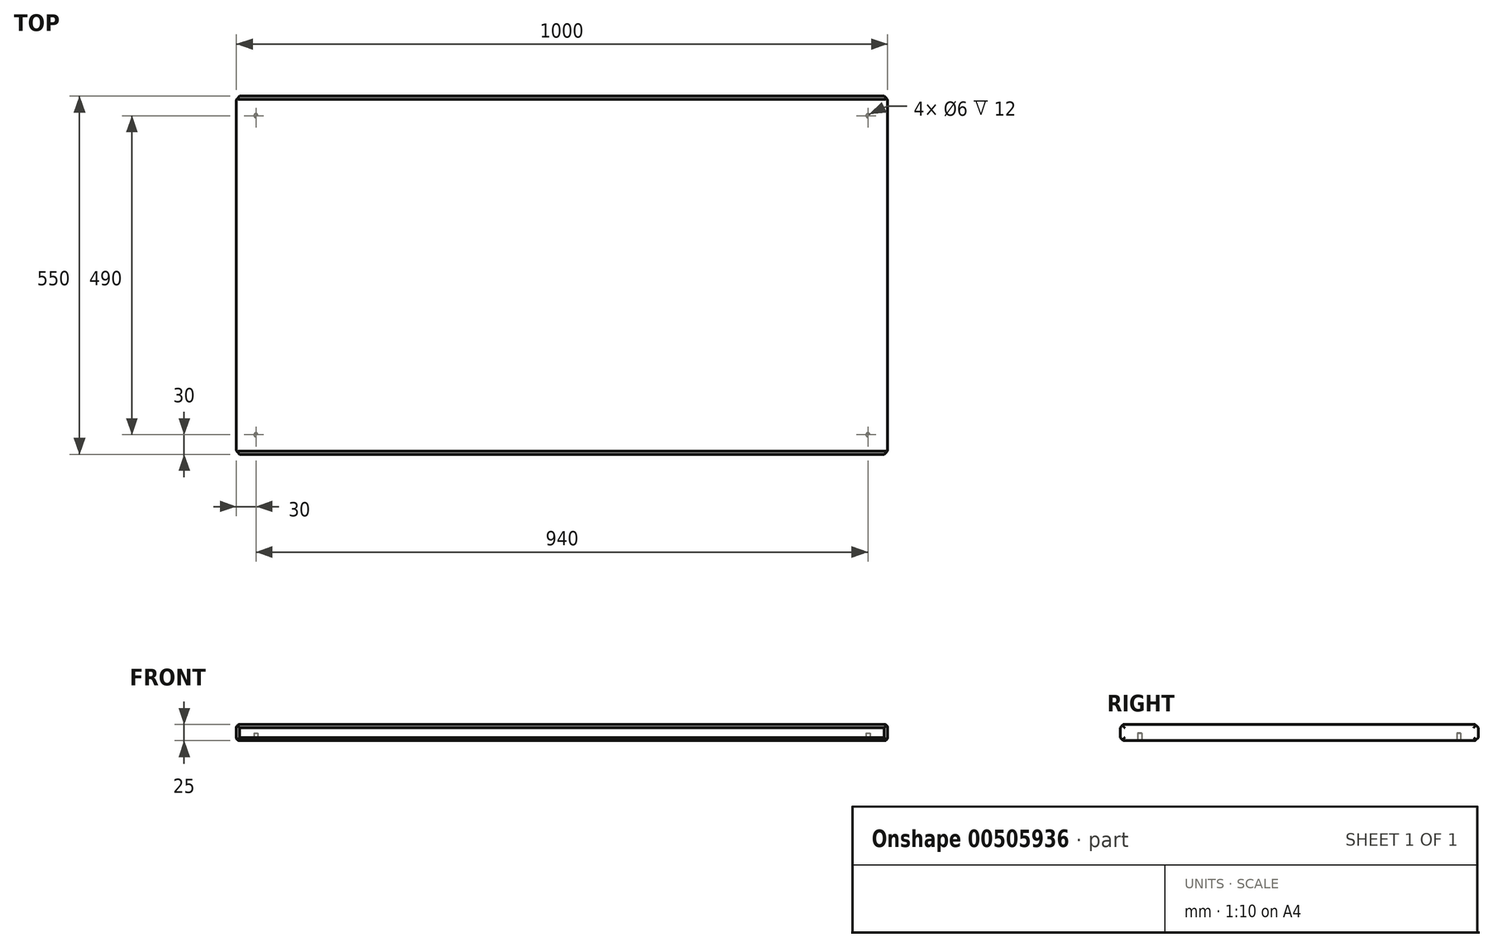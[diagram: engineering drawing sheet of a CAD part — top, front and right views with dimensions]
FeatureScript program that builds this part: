
annotation { "Feature Type Name" : "Feature", "Feature Type Description" : "" }
export const myFeature = defineFeature(function(context is Context, id is Id, definition is map)
    precondition{}
    {
        {
            var Q0;
            Q0=qCreatedBy(makeId("Top.planeOp"),FACE);
            var sketch = newSketch(context, id + "F0", { "sketchPlane" : qUnion([Q0])});
            skLineSegment(sketch, "E0.bottom", {"start": v(500, -275) * mm, "end": v(-500, -275) * mm});
            skLineSegment(sketch, "E0.top", {"start": v(500, 275) * mm, "end": v(-500, 275) * mm});
            skLineSegment(sketch, "E0.left", {"start": v(500, -275) * mm, "end": v(500, 275) * mm});
            skLineSegment(sketch, "E0.right", {"start": v(-500, -275) * mm, "end": v(-500, 275) * mm});
            skPoint(sketch, "E0.middle", {"position": v(0, 0) * mm});
            skSolve(sketch);
        }
        {
            var Q0;
            Q0=makeQuery(id+"F0.imprint","IMPRINT",FACE,{"disambiguationData":[TD([[makeQuery(id+"F0.imprint","IMPRINT",EDGE,{"derivedFrom":sQuery(id+"F0.wireOp",EDGE,"E0.bottom")}),-1.0]])]});
            extrude(context, id + "F1", {"entities" : qUnion([Q0]), "depth" : 25 * mm, "offsetDistance" : 25 * mm});
        }
        {
            var Q0;
            Q0=makeQuery(id+"F1.opExtrude","SWEPT_FACE",FACE,{"disambiguationData":[OSD([sQuery(id+"F0.wireOp",EDGE,"E0.bottom")])]});
            chamfer(context, id + "F2", {"entities" : qUnion([Q0]), "width" : 5 * mm, "tangentPropagation" : true});
        }
        {
            var Q0;
            Q0=makeQuery(id+"F1.opExtrude","SWEPT_FACE",FACE,{"disambiguationData":[OSD([sQuery(id+"F0.wireOp",EDGE,"E0.top")])]});
            chamfer(context, id + "F3", {"entities" : qUnion([Q0]), "width" : 5 * mm, "tangentPropagation" : true});
        }
        {
            var Q0;
            Q0=makeQuery(id+"F1.opExtrude","SWEPT_FACE",FACE,{"disambiguationData":[OSD([sQuery(id+"F0.wireOp",EDGE,"E0.right")])]});
            fillet(context, id + "F4", {"entities" : qUnion([Q0]), "radius" : 5 * mm, "tangentPropagation" : true, "allowEdgeOverflow" : false});
        }
        {
            var Q0;
            Q0=makeQuery(id+"F1.opExtrude","SWEPT_FACE",FACE,{"disambiguationData":[OSD([sQuery(id+"F0.wireOp",EDGE,"E0.left")])]});
            fillet(context, id + "F5", {"entities" : qUnion([Q0]), "radius" : 5 * mm, "tangentPropagation" : true, "allowEdgeOverflow" : false});
        }
        {
            var Q0;
            Q0=makeQuery(id+"F1.opExtrude","CAP_FACE",FACE,{"disambiguationData":[OSD([sQuery(id+"F0.wireOp",EDGE,"E0.bottom"),sQuery(id+"F0.wireOp",EDGE,"E0.top"),sQuery(id+"F0.wireOp",EDGE,"E0.left"),sQuery(id+"F0.wireOp",EDGE,"E0.right")])],"isStart":true});
            var sketch = newSketch(context, id + "F6", { "sketchPlane" : qUnion([Q0])});
            skCircle(sketch, "E1", {"center": v(-470, -245) * mm, "radius": 3 * mm});
            skCircle(sketch, "E2", {"center": v(470, -245) * mm, "radius": 3 * mm});
            skCircle(sketch, "E3", {"center": v(470, 245) * mm, "radius": 3 * mm});
            skCircle(sketch, "E4", {"center": v(-470, 245) * mm, "radius": 3 * mm});
            skSolve(sketch);
        }
        {
            var Q0;
            Q0=makeQuery(id+"F6.imprint","IMPRINT",FACE,{"disambiguationData":[TD([[makeQuery(id+"F6.imprint","IMPRINT",EDGE,{"derivedFrom":sQuery(id+"F6.wireOp",EDGE,"E3")}),1.0]])]});
            extrude(context, id + "F7", {"entities" : qUnion([Q0]), "operationType" : NewBodyOperationType.REMOVE, "oppositeDirection" : true, "depth" : 12 * mm, "offsetDistance" : 25 * mm});
        }
        {
            var Q0;
            Q0=makeQuery(id+"F1.opExtrude","CAP_FACE",FACE,{"disambiguationData":[OSD([sQuery(id+"F0.wireOp",EDGE,"E0.bottom"),sQuery(id+"F0.wireOp",EDGE,"E0.top"),sQuery(id+"F0.wireOp",EDGE,"E0.left"),sQuery(id+"F0.wireOp",EDGE,"E0.right")])],"isStart":true});
            var sketch = newSketch(context, id + "F8", { "sketchPlane" : qUnion([Q0])});
            skCircle(sketch, "E5", {"center": v(470, -245) * mm, "radius": 3 * mm});
            skSolve(sketch);
        }
        {
            var Q0;
            Q0=makeQuery(id+"F8.imprint","IMPRINT",FACE,{"disambiguationData":[TD([[makeQuery(id+"F8.imprint","IMPRINT",EDGE,{"derivedFrom":sQuery(id+"F8.wireOp",EDGE,"E5")}),1.0]])]});
            extrude(context, id + "F9", {"entities" : qUnion([Q0]), "operationType" : NewBodyOperationType.REMOVE, "oppositeDirection" : true, "depth" : 12 * mm, "offsetDistance" : 25 * mm});
        }
        {
            var Q0;
            Q0=makeQuery(id+"F1.opExtrude","CAP_FACE",FACE,{"disambiguationData":[OSD([sQuery(id+"F0.wireOp",EDGE,"E0.bottom"),sQuery(id+"F0.wireOp",EDGE,"E0.top"),sQuery(id+"F0.wireOp",EDGE,"E0.left"),sQuery(id+"F0.wireOp",EDGE,"E0.right")])],"isStart":true});
            var sketch = newSketch(context, id + "F10", { "sketchPlane" : qUnion([Q0])});
            skCircle(sketch, "E6", {"center": v(-470, 245) * mm, "radius": 3 * mm});
            skSolve(sketch);
        }
        {
            var Q0;
            Q0=makeQuery(id+"F10.imprint","IMPRINT",FACE,{"disambiguationData":[TD([[makeQuery(id+"F10.imprint","IMPRINT",EDGE,{"derivedFrom":sQuery(id+"F10.wireOp",EDGE,"E6")}),1.0]])]});
            extrude(context, id + "F11", {"entities" : qUnion([Q0]), "operationType" : NewBodyOperationType.REMOVE, "oppositeDirection" : true, "depth" : 12 * mm, "offsetDistance" : 25 * mm});
        }
        {
            var Q0;
            Q0=makeQuery(id+"F1.opExtrude","CAP_FACE",FACE,{"disambiguationData":[OSD([sQuery(id+"F0.wireOp",EDGE,"E0.bottom"),sQuery(id+"F0.wireOp",EDGE,"E0.top"),sQuery(id+"F0.wireOp",EDGE,"E0.left"),sQuery(id+"F0.wireOp",EDGE,"E0.right")])],"isStart":true});
            var sketch = newSketch(context, id + "F12", { "sketchPlane" : qUnion([Q0])});
            skCircle(sketch, "E7", {"center": v(-470, -245) * mm, "radius": 3 * mm});
            skSolve(sketch);
        }
        {
            var Q0;
            Q0=makeQuery(id+"F12.imprint","IMPRINT",FACE,{"disambiguationData":[TD([[makeQuery(id+"F12.imprint","IMPRINT",EDGE,{"derivedFrom":sQuery(id+"F12.wireOp",EDGE,"E7")}),1.0]])]});
            extrude(context, id + "F13", {"entities" : qUnion([Q0]), "operationType" : NewBodyOperationType.REMOVE, "oppositeDirection" : true, "depth" : 12 * mm, "offsetDistance" : 25 * mm});
        }
    });
